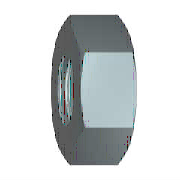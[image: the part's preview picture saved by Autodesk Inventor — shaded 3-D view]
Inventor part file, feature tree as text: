
AUTODESK INVENTOR PART (.ipt)
format: ipt  version: 2025 (Build 290162000, 162)  size: 170,496 bytes
history: native  units: mm (DEFAULTED — no unit token found)
features: extrude x1, chamfer x1, hole x1, other x1, plane x1
ambient origin geometry x7: Origin, YZ Plane, XZ Plane, X Axis, Y Axis, Z Axis, Center Point
bodies: Solid1 (feature_tree)
feature tree (5):
  extrude  "轴承体"  Depth=20.78461mm
  chamfer  "倒角1"  Distance=10.8mm
  hole  "螺纹"  [1 undecoded]
  other  "Work Axis1"
  plane  "Work Plane1"
note: 1 required parameter value undecoded (feature->parameter linkage not recoverable at this tier; creation-order binding heuristic only, values carry confidence <= 0.55)
